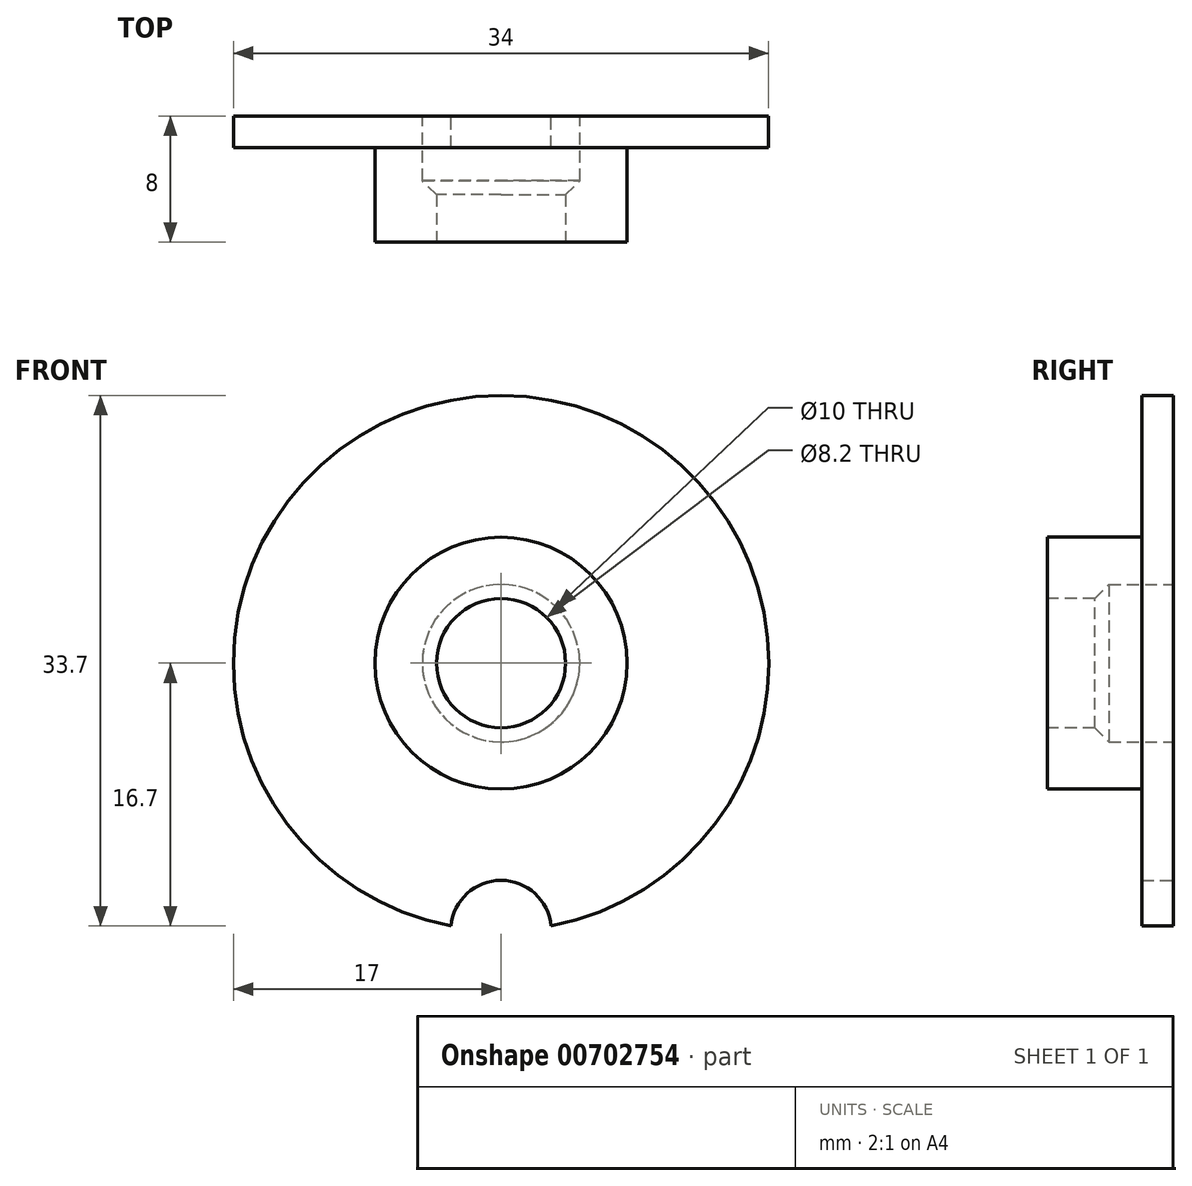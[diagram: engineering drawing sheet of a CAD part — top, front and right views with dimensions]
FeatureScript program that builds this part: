
annotation { "Feature Type Name" : "Feature", "Feature Type Description" : "" }
export const myFeature = defineFeature(function(context is Context, id is Id, definition is map)
    precondition{}
    {
        {
            var Q0;
            Q0=qCreatedBy(makeId("Front.planeOp"),FACE);
            var sketch = newSketch(context, id + "F0", { "sketchPlane" : qUnion([Q0])});
            skCircle(sketch, "E0", {"center": v(0, 0) * mm, "radius": 5 * mm});
            skArc(sketch, "E1", {"start": v(3.19, -16.7) * mm, "mid": v(0, 17) * mm, "end": v(-3.19, -16.7) * mm});
            skArc(sketch, "E2", {"start": v(3.19, -16.7) * mm, "mid": v(0, -13.8) * mm, "end": v(-3.19, -16.7) * mm});
            skSolve(sketch);
        }
        {
            var Q0;
            Q0=qSketchRegion(id+"F0",true);
            extrude(context, id + "F1", {"entities" : qUnion([Q0]), "depth" : 2 * mm, "offsetDistance" : 25 * mm});
        }
        {
            var Q0;
            Q0=qCreatedBy(makeId("Front.planeOp"),FACE);
            var sketch = newSketch(context, id + "F2", { "sketchPlane" : qUnion([Q0])});
            skCircle(sketch, "E3.0", {"center": v(0, 0) * mm, "radius": 5 * mm});
            skCircle(sketch, "E4", {"center": v(0, 0) * mm, "radius": 8 * mm});
            skSolve(sketch);
        }
        {
            var Q0;
            Q0=qSketchRegion(id+"F2",true);
            extrude(context, id + "F3", {"entities" : qUnion([Q0]), "operationType" : NewBodyOperationType.ADD, "depth" : 8 * mm, "offsetDistance" : 25 * mm});
        }
        {
            var Q0;
            Q0=makeQuery(id+"F3.opExtrude","CAP_FACE",FACE,{"disambiguationData":[OSD([sQuery(id+"F2.wireOp",EDGE,"E3.0"),sQuery(id+"F2.wireOp",EDGE,"E4")])],"isStart":false});
            var sketch = newSketch(context, id + "F4", { "sketchPlane" : qUnion([Q0])});
            skCircle(sketch, "E5.0", {"center": v(0, 0) * mm, "radius": 5 * mm});
            skCircle(sketch, "E6", {"center": v(0, 0) * mm, "radius": 4.1 * mm});
            skSolve(sketch);
        }
        {
            var Q0;
            Q0=qSketchRegion(id+"F4",true);
            extrude(context, id + "F5", {"entities" : qUnion([Q0]), "operationType" : NewBodyOperationType.ADD, "oppositeDirection" : true, "depth" : 4 * mm, "offsetDistance" : 25 * mm});
        }
        {
            var Q0;
            Q0=makeQuery(id+"F5.opExtrude","CAP_EDGE",EDGE,{"disambiguationData":[OSD([sQuery(id+"F4.wireOp",EDGE,"E6")])],"isStart":false});
            chamfer(context, id + "F6", {"entities" : qUnion([Q0]), "width" : 1 * mm, "tangentPropagation" : true});
        }
    });
